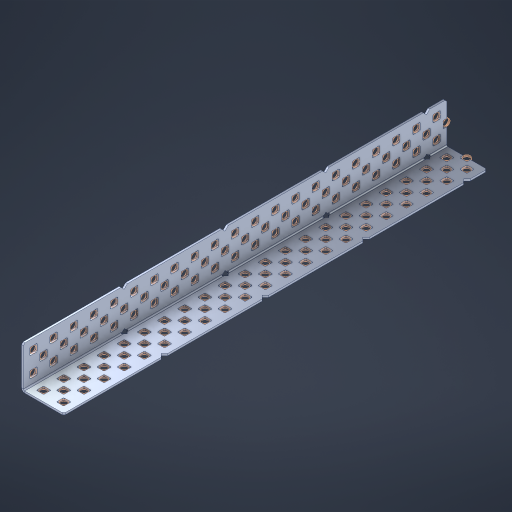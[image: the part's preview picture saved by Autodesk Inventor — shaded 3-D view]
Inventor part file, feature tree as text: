
AUTODESK INVENTOR PART (.ipt)
format: ipt  version: 2023 (Build 270158000, 158)  size: 1,597,952 bytes
history: native  units: in
note: dims shown in document units (in); Inventor stores cm internally (conversion verified against a paired STEP export)
features: other x132, extrude x124, sheet_metal_op x8, sketch x7, pattern_linear x2, mirror x1, chamfer x1
ambient origin geometry x8: Origin, YZ Plane, XZ Plane, XY Plane, X Axis, Y Axis, Z Axis, Center Point
bodies: Solid1 (feature_tree), Body (feature_tree)
feature tree (275):
  sheet_metal_op  "Flanges"
  sheet_metal_op  "Body Pattern"
  pattern_linear  "Center Pattern"  Spacing1=1.0in  [1 undecoded]
  other  "Arc Length"
  pattern_linear  "Notch Pattern"  Spacing1=0.1875in  [1 undecoded]
  other  "Diagonal Plane"
  mirror  "Everything Mirrored"
  chamfer  "End Chamfer"
  sketch  "Sketch1"  dims[d0=1.0in]
  other  "Plate1"
  sketch  "Sketch2"  dims[d1=10.5in]
  other  "Plate2"
  sheet_metal_op  "Bend1"
  sheet_metal_op  "Corner1"
  sketch  "Sketch8"  dims[d2=0.0469in]
  sketch  "Sketch9"  dims[d3=0.0469in]
  other  "Srf91"
  sheet_metal_op  "Body Pattern Sketch"
  other  "Srf92"
  sketch  "Sketch13"  dims[d4=0.0234in]
  sketch  "Sketch15"  dims[d5=0.0938in]
  sketch  "Sketch16"  dims[d6=0.0469in d7=1.0in d8=90.0deg d9=0.0312in d10=0.1875in d11=0.0469in d12=0.0469in d49=0.182in d50=0.02in d52=0.25in d53=0.0469in d54=0.0in d55=0.172in d56=1.0in d57=0.0in d60=8.2677in d62=0.5in d63=0.7874in d65=0.5in d85=0.1473in d86=0.1659in d89=0.0469in d90=0.0in d91=0.04in d92=0.0491in d95=2.5in d96=0.04in d97=0.25in d98=45.0deg d99=0.25in d106=0.182in d107=0.02in d108=0.5in d110=0.0469in d111=0.0in d112=0.172in d113=0.5in d114=0.0in d117=0.5in d123=0.25in d125=0.25in d126=0.0491in d127=0.1227in d128=0.08in d129=0.04in d130=2.5in]
  other  "Srf786"
  other  "Srf856"
  other  "Srf857"
  other  "Srf858"
  other  "Srf859"
  other  "Srf860"
  other  "Srf861"
  other  "Srf889"
  other  "Srf890"
  other  "Srf891"
  other  "Srf1275"
  other  "Srf1276"
  other  "Srf1278"
  other  "Srf1279"
  other  "Srf1280"
  other  "Srf1281"
  other  "Srf1282"
  other  "Srf1283"
  other  "Srf1277"
  other  "Srf1285"
  other  "Srf1286"
  other  "Srf1287"
  other  "Srf1383"
  other  "Srf1384"
  other  "Srf1385"
  other  "Srf1386"
  other  "Srf1387"
  other  "Srf1388"
  other  "Srf1389"
  other  "Srf1390"
  other  "Srf1391"
  other  "Srf1392"
  other  "Srf1393"
  other  "Srf1394"
  other  "Srf1395"
  other  "Srf1396"
  other  "Srf1397"
  other  "Srf1398"
  other  "Srf1399"
  other  "Srf1400"
  other  "Srf1401"
  other  "Srf1402"
  other  "Srf1403"
  other  "Srf1404"
  other  "Srf1405"
  other  "Srf1406"
  other  "Srf1407"
  other  "Srf1408"
  other  "Srf1409"
  other  "Srf1410"
  other  "Srf1411"
  other  "Srf1412"
  other  "Srf1413"
  other  "Srf1414"
  other  "Srf1415"
  other  "Srf1416"
  other  "Srf1445"
  other  "Srf1446"
  other  "Srf1447"
  other  "Srf1448"
  other  "Srf1449"
  other  "Srf1450"
  other  "Srf1451"
  other  "Srf1452"
  other  "Srf1453"
  other  "Srf1454"
  other  "Srf1455"
  other  "Srf1456"
  other  "Srf1457"
  other  "Srf1458"
  other  "Srf1459"
  other  "Srf1460"
  other  "Srf1461"
  other  "Srf1475"
  other  "Srf1476"
  other  "Srf1477"
  other  "Srf1478"
  other  "Srf1479"
  other  "Srf1480"
  other  "Srf1481"
  other  "Srf1482"
  other  "Srf1483"
  other  "Srf1484"
  other  "Srf1485"
  other  "Srf1486"
  other  "Srf1487"
  other  "Srf1488"
  other  "Srf1489"
  other  "Srf1490"
  other  "Srf1491"
  other  "Srf1492"
  other  "Srf1493"
  other  "Srf1494"
  other  "Srf1495"
  other  "Srf1496"
  other  "Srf1497"
  other  "Srf1498"
  other  "Srf1499"
  other  "Srf1500"
  other  "Srf1501"
  other  "Srf1502"
  other  "Srf1503"
  other  "Srf1504"
  other  "Srf1505"
  other  "Srf1506"
  other  "Srf1507"
  other  "Srf1508"
  other  "Srf1537"
  other  "Srf1538"
  other  "Srf1539"
  other  "Srf1540"
  other  "Srf1541"
  other  "Srf1542"
  other  "Srf1543"
  other  "Srf1544"
  other  "Srf1545"
  other  "Srf1546"
  other  "Srf1547"
  other  "Srf1548"
  other  "Srf1549"
  other  "Srf1550"
  other  "Srf1551"
  other  "Srf1552"
  other  "Srf1553"
  sheet_metal_op  "Body Stamp"
  sheet_metal_op  "Body Circle"
  other  "Center Stamp"
  other  "Center Circle"
  sheet_metal_op  "Notch"
  extrude  "ExtrusionSrf92"  Depth=0.0469in
  extrude  "ExtrusionSrf856"  Depth=0.0469in
  extrude  "ExtrusionSrf857"  Depth=0.182in
  extrude  "ExtrusionSrf858"  Depth=0.02in
  extrude  "ExtrusionSrf859"  Depth=0.25in
  extrude  "ExtrusionSrf860"  Depth=0.0469in
  extrude  "ExtrusionSrf861"  TaperAngle=0.0deg  [1 undecoded]
  extrude  "ExtrusionSrf889"  Depth=2.5in
  extrude  "ExtrusionSrf890"  Depth=1.0in TaperAngle=0.0deg
  extrude  "ExtrusionSrf891"  Depth=2.5in
  extrude  "ExtrusionSrf1275"  Depth=0.5in
  extrude  "ExtrusionSrf1276"  Depth=2.5in
  extrude  "ExtrusionSrf1277"  Depth=2.5in
  extrude  "ExtrusionSrf1278"  Depth=0.0469in
  extrude  "ExtrusionSrf1279"  Depth=2.5in TaperAngle=0.0deg
  extrude  "ExtrusionSrf1280"  Depth=2.5in
  extrude  "ExtrusionSrf1281"  Depth=0.25in TaperAngle=45.0deg
  extrude  "ExtrusionSrf1282"  Depth=0.25in
  extrude  "ExtrusionSrf1345"  Depth=0.182in
  extrude  "ExtrusionSrf1346"  Depth=0.02in
  extrude  "ExtrusionSrf1347"  Depth=0.5in
  extrude  "ExtrusionSrf1348"  Depth=0.0469in
  extrude  "ExtrusionSrf1383"  TaperAngle=0.0deg  [1 undecoded]
  extrude  "ExtrusionSrf1384"  Depth=2.5in
  extrude  "ExtrusionSrf1385"  Depth=0.5in TaperAngle=0.0deg
  extrude  "ExtrusionSrf1386"  Depth=0.5in
  extrude  "ExtrusionSrf1387"  Depth=0.25in
  extrude  "ExtrusionSrf1388"  Depth=0.25in
  extrude  "ExtrusionSrf1389"  Depth=2.5in
  extrude  "ExtrusionSrf1390"  Depth=2.5in
  extrude  "ExtrusionSrf1391"  Depth=2.5in
  extrude  "ExtrusionSrf1392"  Depth=2.5in
  extrude  "ExtrusionSrf1393"  Depth=2.5in
  extrude  "ExtrusionSrf1394"  [1 undecoded]
  extrude  "ExtrusionSrf1395"  [1 undecoded]
  extrude  "ExtrusionSrf1396"  [1 undecoded]
  extrude  "ExtrusionSrf1397"  [1 undecoded]
  extrude  "ExtrusionSrf1398"  [1 undecoded]
  extrude  "ExtrusionSrf1399"  [1 undecoded]
  extrude  "ExtrusionSrf1400"  [1 undecoded]
  extrude  "ExtrusionSrf1401"  [1 undecoded]
  extrude  "ExtrusionSrf1402"  [1 undecoded]
  extrude  "ExtrusionSrf1403"  [1 undecoded]
  extrude  "ExtrusionSrf1404"  [1 undecoded]
  extrude  "ExtrusionSrf1405"  [1 undecoded]
  extrude  "ExtrusionSrf1406"  [1 undecoded]
  extrude  "ExtrusionSrf1407"  [1 undecoded]
  extrude  "ExtrusionSrf1408"  [1 undecoded]
  extrude  "ExtrusionSrf1409"  [1 undecoded]
  extrude  "ExtrusionSrf1410"  [1 undecoded]
  extrude  "ExtrusionSrf1411"  [1 undecoded]
  extrude  "ExtrusionSrf1412"  [1 undecoded]
  extrude  "ExtrusionSrf1413"  [1 undecoded]
  extrude  "ExtrusionSrf1414"  [1 undecoded]
  extrude  "ExtrusionSrf1415"  [1 undecoded]
  extrude  "ExtrusionSrf1416"  [1 undecoded]
  extrude  "ExtrusionSrf1445"  [1 undecoded]
  extrude  "ExtrusionSrf1446"  [1 undecoded]
  extrude  "ExtrusionSrf1447"  [1 undecoded]
  extrude  "ExtrusionSrf1448"  [1 undecoded]
  extrude  "ExtrusionSrf1449"  [1 undecoded]
  extrude  "ExtrusionSrf1450"  [1 undecoded]
  extrude  "ExtrusionSrf1451"  [1 undecoded]
  extrude  "ExtrusionSrf1452"  [1 undecoded]
  extrude  "ExtrusionSrf1453"  [1 undecoded]
  extrude  "ExtrusionSrf1454"  [1 undecoded]
  extrude  "ExtrusionSrf1455"  [1 undecoded]
  extrude  "ExtrusionSrf1456"  [1 undecoded]
  extrude  "ExtrusionSrf1457"  [1 undecoded]
  extrude  "ExtrusionSrf1458"  [1 undecoded]
  extrude  "ExtrusionSrf1459"  [1 undecoded]
  extrude  "ExtrusionSrf1460"  [1 undecoded]
  extrude  "ExtrusionSrf1461"  [1 undecoded]
  extrude  "ExtrusionSrf1475"  [1 undecoded]
  extrude  "ExtrusionSrf1476"  [1 undecoded]
  extrude  "ExtrusionSrf1477"  [1 undecoded]
  extrude  "ExtrusionSrf1478"  [1 undecoded]
  extrude  "ExtrusionSrf1479"  [1 undecoded]
  extrude  "ExtrusionSrf1480"  [1 undecoded]
  extrude  "ExtrusionSrf1481"  [1 undecoded]
  extrude  "ExtrusionSrf1482"  [1 undecoded]
  extrude  "ExtrusionSrf1483"  [1 undecoded]
  extrude  "ExtrusionSrf1484"  [1 undecoded]
  extrude  "ExtrusionSrf1485"  [1 undecoded]
  extrude  "ExtrusionSrf1486"  [1 undecoded]
  extrude  "ExtrusionSrf1487"  [1 undecoded]
  extrude  "ExtrusionSrf1488"  [1 undecoded]
  extrude  "ExtrusionSrf1489"  [1 undecoded]
  extrude  "ExtrusionSrf1490"  [1 undecoded]
  extrude  "ExtrusionSrf1491"  [1 undecoded]
  extrude  "ExtrusionSrf1492"  [1 undecoded]
  extrude  "ExtrusionSrf1493"  [1 undecoded]
  extrude  "ExtrusionSrf1494"  [1 undecoded]
  extrude  "ExtrusionSrf1495"  [1 undecoded]
  extrude  "ExtrusionSrf1496"  [1 undecoded]
  extrude  "ExtrusionSrf1497"  [1 undecoded]
  extrude  "ExtrusionSrf1498"  [1 undecoded]
  extrude  "ExtrusionSrf1499"  [1 undecoded]
  extrude  "ExtrusionSrf1500"  [1 undecoded]
  extrude  "ExtrusionSrf1501"  [1 undecoded]
  extrude  "ExtrusionSrf1502"  [1 undecoded]
  extrude  "ExtrusionSrf1503"  [1 undecoded]
  extrude  "ExtrusionSrf1504"  [1 undecoded]
  extrude  "ExtrusionSrf1505"  [1 undecoded]
  extrude  "ExtrusionSrf1506"  [1 undecoded]
  extrude  "ExtrusionSrf1507"  [1 undecoded]
  extrude  "ExtrusionSrf1508"  [1 undecoded]
  extrude  "ExtrusionSrf1537"  [1 undecoded]
  extrude  "ExtrusionSrf1538"  [1 undecoded]
  extrude  "ExtrusionSrf1539"  [1 undecoded]
  extrude  "ExtrusionSrf1540"  [1 undecoded]
  extrude  "ExtrusionSrf1541"  [1 undecoded]
  extrude  "ExtrusionSrf1542"  [1 undecoded]
  extrude  "ExtrusionSrf1543"  [1 undecoded]
  extrude  "ExtrusionSrf1544"  [1 undecoded]
  extrude  "ExtrusionSrf1545"  [1 undecoded]
  extrude  "ExtrusionSrf1546"  [1 undecoded]
  extrude  "ExtrusionSrf1547"  [1 undecoded]
  extrude  "ExtrusionSrf1548"  [1 undecoded]
  extrude  "ExtrusionSrf1549"  [1 undecoded]
  extrude  "ExtrusionSrf1550"  [1 undecoded]
  extrude  "ExtrusionSrf1551"  [1 undecoded]
  extrude  "ExtrusionSrf1552"  [1 undecoded]
  extrude  "ExtrusionSrf1553"  [1 undecoded]
note: 95 required parameter values undecoded (feature->parameter linkage not recoverable at this tier; creation-order binding heuristic only, values carry confidence <= 0.55)
